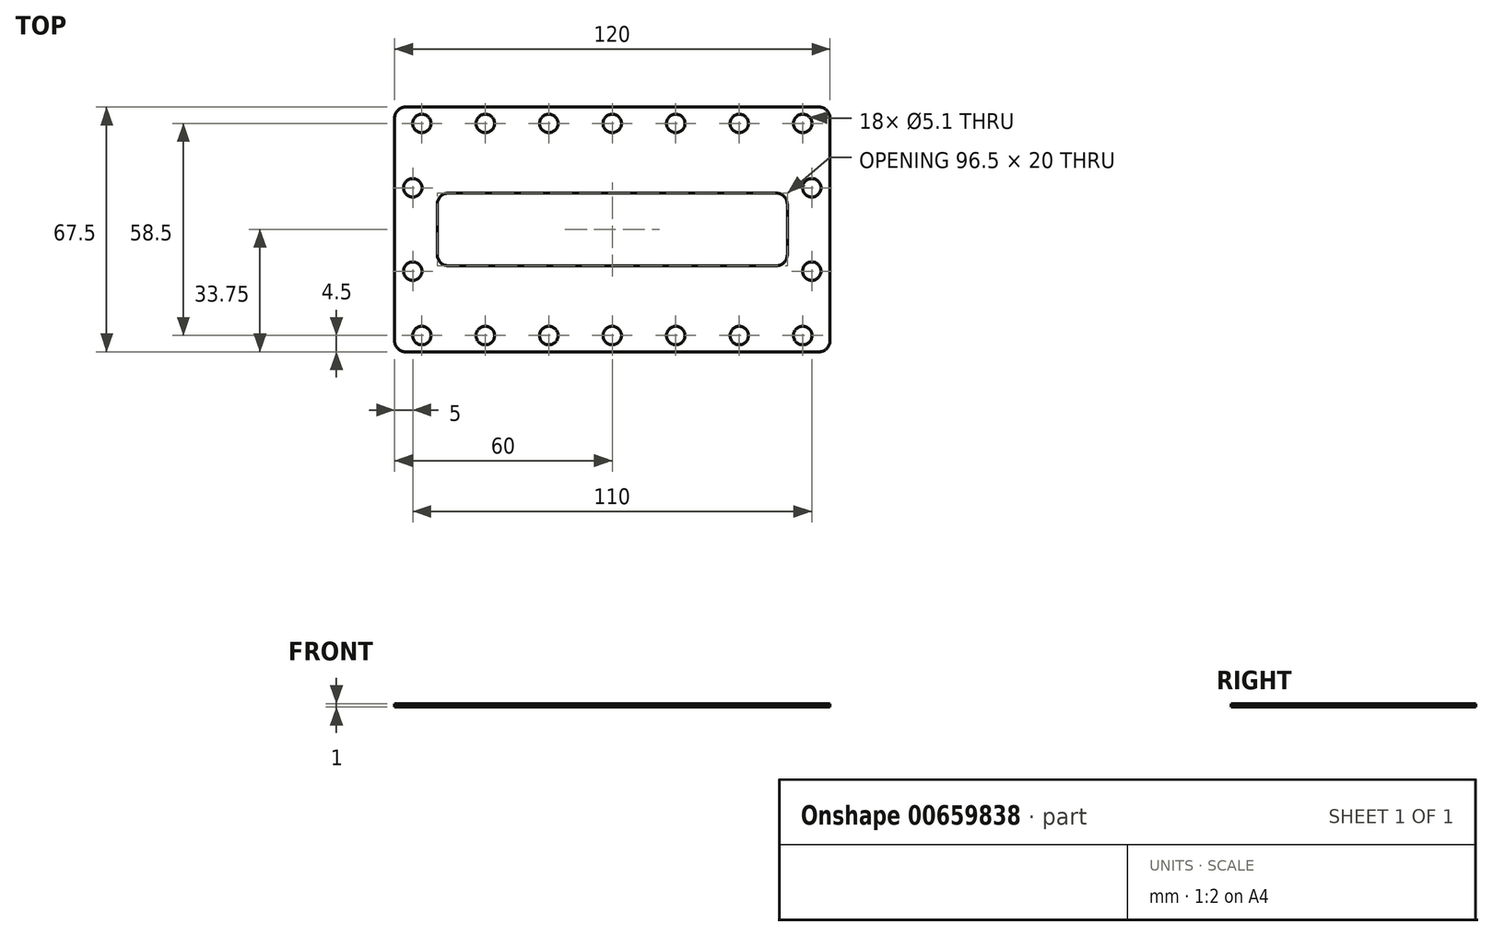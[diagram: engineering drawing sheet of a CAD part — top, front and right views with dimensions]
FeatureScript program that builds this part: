
annotation { "Feature Type Name" : "Feature", "Feature Type Description" : "" }
export const myFeature = defineFeature(function(context is Context, id is Id, definition is map)
    precondition{}
    {
        {
            var Q0;
            Q0=qCreatedBy(makeId("Top.planeOp"),FACE);
            var sketch = newSketch(context, id + "F0", { "sketchPlane" : qUnion([Q0])});
            skLineSegment(sketch, "E0.bottom", {"start": v(0, 0) * mm, "end": v(120, 0) * mm});
            skLineSegment(sketch, "E0.top", {"start": v(0, -67.5) * mm, "end": v(120, -67.5) * mm});
            skLineSegment(sketch, "E0.left", {"start": v(0, 0) * mm, "end": v(0, -67.5) * mm});
            skLineSegment(sketch, "E0.right", {"start": v(120, 0) * mm, "end": v(120, -67.5) * mm});
            skSolve(sketch);
        }
        {
            var Q0;
            Q0 = qSketchRegion(id + "F0", true);
            extrude(context, id + "F1", {"entities" : qUnion([Q0]), "depth" : 1 * mm, "offsetDistance" : 25 * mm});
        }
        {
            var Q0;
            Q0=makeQuery(id+"F1.opExtrude","CAP_FACE",FACE,{"disambiguationData":[OSD([sQuery(id+"F0.wireOp",EDGE,"E0.bottom"),sQuery(id+"F0.wireOp",EDGE,"E0.top"),sQuery(id+"F0.wireOp",EDGE,"E0.left"),sQuery(id+"F0.wireOp",EDGE,"E0.right")])],"isStart":false});
            var sketch = newSketch(context, id + "F2", { "sketchPlane" : qUnion([Q0])});
            skLineSegment(sketch, "E1.bottom", {"start": v(14.75, -23.75) * mm, "end": v(105.25, -23.75) * mm});
            skLineSegment(sketch, "E1.top", {"start": v(14.75, -43.75) * mm, "end": v(105.25, -43.75) * mm});
            skLineSegment(sketch, "E1.left", {"start": v(11.75, -26.75) * mm, "end": v(11.75, -40.75) * mm});
            skLineSegment(sketch, "E1.right", {"start": v(108.25, -26.75) * mm, "end": v(108.25, -40.75) * mm});
            skPoint(sketch, "E2.visualSharp", {"position": v(11.75, -23.75) * mm});
            skArc(sketch, "E2.filletArc", {"start": v(14.75, -23.75) * mm, "mid": v(12.63, -24.63) * mm, "end": v(11.75, -26.75) * mm});
            skPoint(sketch, "E3.visualSharp", {"position": v(11.75, -43.75) * mm});
            skArc(sketch, "E3.filletArc", {"start": v(11.75, -40.75) * mm, "mid": v(12.63, -42.87) * mm, "end": v(14.75, -43.75) * mm});
            skPoint(sketch, "E4.visualSharp", {"position": v(108.25, -43.75) * mm});
            skArc(sketch, "E4.filletArc", {"start": v(105.25, -43.75) * mm, "mid": v(107.37, -42.87) * mm, "end": v(108.25, -40.75) * mm});
            skPoint(sketch, "E5.visualSharp", {"position": v(108.25, -23.75) * mm});
            skArc(sketch, "E5.filletArc", {"start": v(108.25, -26.75) * mm, "mid": v(107.37, -24.63) * mm, "end": v(105.25, -23.75) * mm});
            skCircle(sketch, "E6", {"center": v(7.5, -4.5) * mm, "radius": 2.55 * mm});
            skCircle(sketch, "E7.0.1.0", {"center": v(7.5, -63) * mm, "radius": 2.55 * mm});
            skCircle(sketch, "E7.1.0.0", {"center": v(25, -4.5) * mm, "radius": 2.55 * mm});
            skCircle(sketch, "E7.1.1.0", {"center": v(25, -63) * mm, "radius": 2.55 * mm});
            skCircle(sketch, "E7.2.0.0", {"center": v(42.5, -4.5) * mm, "radius": 2.55 * mm});
            skCircle(sketch, "E7.2.1.0", {"center": v(42.5, -63) * mm, "radius": 2.55 * mm});
            skCircle(sketch, "E7.3.0.0", {"center": v(60, -4.5) * mm, "radius": 2.55 * mm});
            skCircle(sketch, "E7.3.1.0", {"center": v(60, -63) * mm, "radius": 2.55 * mm});
            skCircle(sketch, "E7.4.0.0", {"center": v(77.5, -4.5) * mm, "radius": 2.55 * mm});
            skCircle(sketch, "E7.4.1.0", {"center": v(77.5, -63) * mm, "radius": 2.55 * mm});
            skCircle(sketch, "E7.5.0.0", {"center": v(95, -4.5) * mm, "radius": 2.55 * mm});
            skCircle(sketch, "E7.5.1.0", {"center": v(95, -63) * mm, "radius": 2.55 * mm});
            skCircle(sketch, "E7.6.0.0", {"center": v(112.5, -4.5) * mm, "radius": 2.55 * mm});
            skCircle(sketch, "E7.6.1.0", {"center": v(112.5, -63) * mm, "radius": 2.55 * mm});
            skLineSegment(sketch, "E7.direction1", {"start": v(7.5, -4.5) * mm, "end": v(25, -4.5) * mm, "construction": true});
            skLineSegment(sketch, "E7.direction2", {"start": v(7.5, -4.5) * mm, "end": v(7.5, -63) * mm, "construction": true});
            skSolve(sketch);
        }
        {
            var Q0;
            Q0 = qSketchRegion(id + "F2", true);
            extrude(context, id + "F3", {"entities" : qUnion([Q0]), "operationType" : NewBodyOperationType.REMOVE, "oppositeDirection" : true, "depth" : 25 * mm, "offsetDistance" : 25 * mm});
        }
        {
            var Q0;
            Q0=makeQuery(id+"F1.opExtrude","SWEPT_EDGE",EDGE,{"disambiguationData":[OSD([sQuery(id+"F0.wireOp",EDGE,"E0.bottom"),sQuery(id+"F0.wireOp",EDGE,"E0.left")])]});
            var Q1;
            Q1=makeQuery(id+"F1.opExtrude","SWEPT_EDGE",EDGE,{"disambiguationData":[OSD([sQuery(id+"F0.wireOp",EDGE,"E0.top"),sQuery(id+"F0.wireOp",EDGE,"E0.left")])]});
            var Q2;
            Q2=makeQuery(id+"F1.opExtrude","SWEPT_EDGE",EDGE,{"disambiguationData":[OSD([sQuery(id+"F0.wireOp",EDGE,"E0.bottom"),sQuery(id+"F0.wireOp",EDGE,"E0.right")])]});
            var Q3;
            Q3=makeQuery(id+"F1.opExtrude","SWEPT_EDGE",EDGE,{"disambiguationData":[OSD([sQuery(id+"F0.wireOp",EDGE,"E0.top"),sQuery(id+"F0.wireOp",EDGE,"E0.right")])]});
            fillet(context, id + "F4", {"entities" : qUnion([Q0, Q1, Q2, Q3]), "radius" : 3 * mm, "tangentPropagation" : true, "allowEdgeOverflow" : false});
        }
        {
            var Q0;
            Q0=makeQuery(id+"F1.opExtrude","CAP_FACE",FACE,{"disambiguationData":[OSD([sQuery(id+"F0.wireOp",EDGE,"E0.bottom"),sQuery(id+"F0.wireOp",EDGE,"E0.top"),sQuery(id+"F0.wireOp",EDGE,"E0.left"),sQuery(id+"F0.wireOp",EDGE,"E0.right")])],"isStart":false});
            var sketch = newSketch(context, id + "F5", { "sketchPlane" : qUnion([Q0])});
            skCircle(sketch, "E8", {"center": v(115, -45.25) * mm, "radius": 2.55 * mm});
            skCircle(sketch, "E9.0.1.0", {"center": v(115, -22.25) * mm, "radius": 2.55 * mm});
            skCircle(sketch, "E9.1.0.0", {"center": v(5, -45.25) * mm, "radius": 2.55 * mm});
            skCircle(sketch, "E9.1.1.0", {"center": v(5, -22.25) * mm, "radius": 2.55 * mm});
            skLineSegment(sketch, "E9.direction1", {"start": v(115, -45.25) * mm, "end": v(5, -45.25) * mm, "construction": true});
            skLineSegment(sketch, "E9.direction2", {"start": v(115, -45.25) * mm, "end": v(115, -22.25) * mm, "construction": true});
            skSolve(sketch);
        }
        {
            var Q0;
            Q0 = qSketchRegion(id + "F5", true);
            extrude(context, id + "F6", {"entities" : qUnion([Q0]), "operationType" : NewBodyOperationType.REMOVE, "oppositeDirection" : true, "depth" : 25 * mm, "offsetDistance" : 25 * mm});
        }
    });
